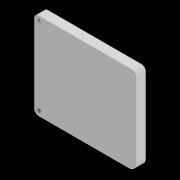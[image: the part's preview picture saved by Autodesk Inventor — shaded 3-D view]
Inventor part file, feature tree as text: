
AUTODESK INVENTOR PART (.ipt)
format: ipt  version: 2020 (Build 240168000, 168)  size: 93,184 bytes
history: native  units: in
note: dims shown in document units (in); Inventor stores cm internally (conversion verified against a paired STEP export)
features: extrude x1, imported_body x1
ambient origin geometry x8: Origin, YZ Plane, XZ Plane, XY Plane, X Axis, Y Axis, Z Axis, Center Point
bodies: Solid1 (feature_tree)
feature tree (2):
  extrude  "BaseFeature"  Depth=0.126in TaperAngle=0.0deg
  imported_body  "Base"
